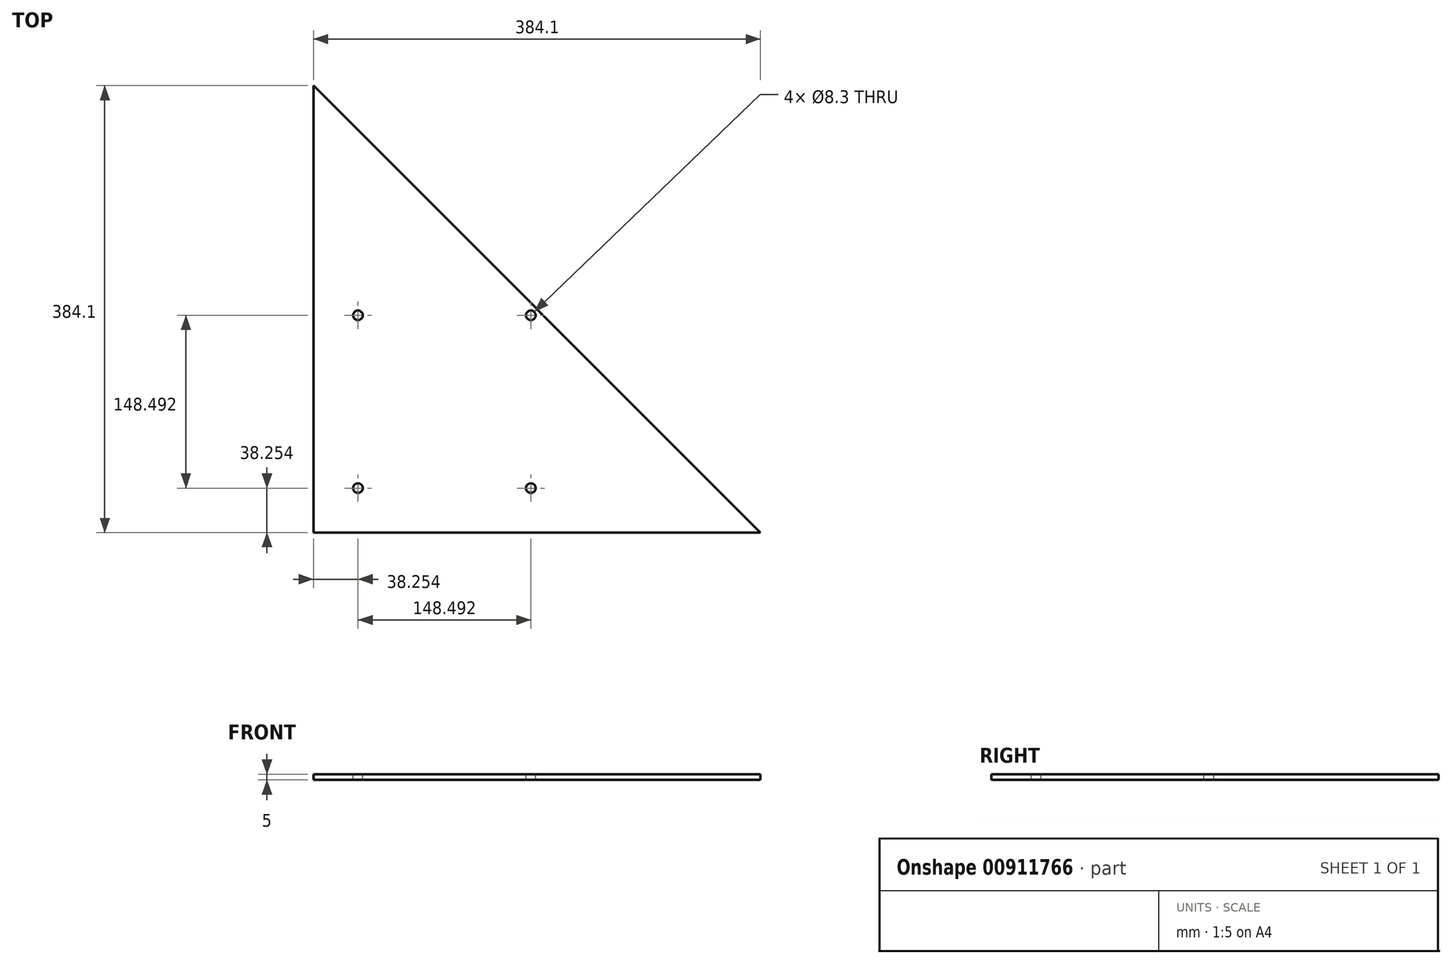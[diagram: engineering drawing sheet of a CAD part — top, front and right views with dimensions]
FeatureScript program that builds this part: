
annotation { "Feature Type Name" : "Feature", "Feature Type Description" : "" }
export const myFeature = defineFeature(function(context is Context, id is Id, definition is map)
    precondition{}
    {
        {
            var Q0;
            Q0=qCreatedBy(makeId("Top.planeOp"),FACE);
            var sketch = newSketch(context, id + "F0", { "sketchPlane" : qUnion([Q0])});
            skLineSegment(sketch, "E0", {"start": v(0, 384.1) * mm, "end": v(0, 0) * mm});
            skLineSegment(sketch, "E1", {"start": v(0, 0) * mm, "end": v(384.1, 0) * mm});
            skLineSegment(sketch, "E2", {"start": v(384.1, 0) * mm, "end": v(0, 384.1) * mm});
            skSolve(sketch);
        }
        {
            var Q0;
            Q0=makeQuery(id+"F0.imprint","IMPRINT",FACE,{"disambiguationData":[TD([[makeQuery(id+"F0.imprint","IMPRINT",EDGE,{"derivedFrom":sQuery(id+"F0.wireOp",EDGE,"E0")}),1.0]])]});
            extrude(context, id + "F1", {"entities" : qUnion([Q0]), "depth" : 5 * mm, "offsetDistance" : 25 * mm});
        }
        {
            var Q0;
            Q0=makeQuery(id+"F1.opExtrude","CAP_FACE",FACE,{"disambiguationData":[OSD([sQuery(id+"F0.wireOp",EDGE,"E0"),sQuery(id+"F0.wireOp",EDGE,"E1"),sQuery(id+"F0.wireOp",EDGE,"E2")])],"isStart":false});
            var sketch = newSketch(context, id + "F2", { "sketchPlane" : qUnion([Q0])});
            skPoint(sketch, "E3", {"position": v(38.25, 38.25) * mm});
            skPoint(sketch, "E4", {"position": v(38.25, 186.75) * mm});
            skPoint(sketch, "E5", {"position": v(186.75, 38.25) * mm});
            skPoint(sketch, "E6", {"position": v(186.75, 186.75) * mm});
            skCircle(sketch, "E7", {"center": v(38.25, 186.75) * mm, "radius": 4.15 * mm});
            skCircle(sketch, "E8", {"center": v(186.75, 186.75) * mm, "radius": 4.15 * mm});
            skCircle(sketch, "E9", {"center": v(186.75, 38.25) * mm, "radius": 4.15 * mm});
            skCircle(sketch, "E10", {"center": v(38.25, 38.25) * mm, "radius": 4.15 * mm});
            skSolve(sketch);
        }
        {
            var Q0;
            Q0=qSketchRegion(id+"F2",true);
            extrude(context, id + "F3", {"entities" : qUnion([Q0]), "operationType" : NewBodyOperationType.REMOVE, "oppositeDirection" : true, "depth" : 25 * mm, "offsetDistance" : 25 * mm});
        }
    });
